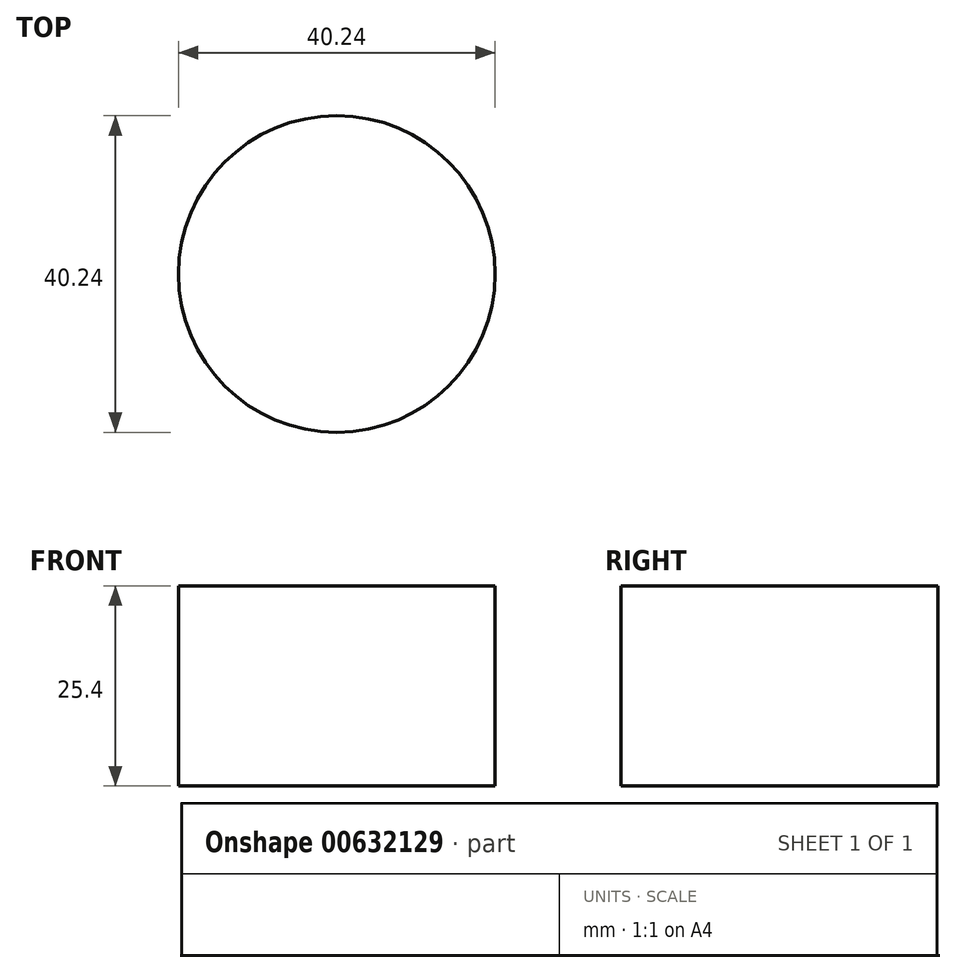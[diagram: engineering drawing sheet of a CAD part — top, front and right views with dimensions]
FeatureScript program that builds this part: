
annotation { "Feature Type Name" : "Feature", "Feature Type Description" : "" }
export const myFeature = defineFeature(function(context is Context, id is Id, definition is map)
    precondition{}
    {
        {
            var Q0;
            Q0=qCreatedBy(makeId("Top.planeOp"),FACE);
            var sketch = newSketch(context, id + "F0", { "sketchPlane" : qUnion([Q0])});
            skCircle(sketch, "E0", {"center": v(0, 0) * mm, "radius": 20.12 * mm});
            skLineSegment(sketch, "E1", {"start": v(-38.95, -13.39) * mm, "end": v(8.38, 39.55) * mm});
            skSolve(sketch);
        }
        {
            var Q0;
            Q0=sQuery(id+"F0.wireOp",EDGE,"E0");
            extrude(context, id + "F1", {"bodyType" : ToolBodyType.SURFACE, "surfaceEntities" : qUnion([Q0]), "endBound" : BoundingType.SYMMETRIC, "depth" : 25.4 * mm, "offsetDistance" : 25.4 * mm});
        }
    });
